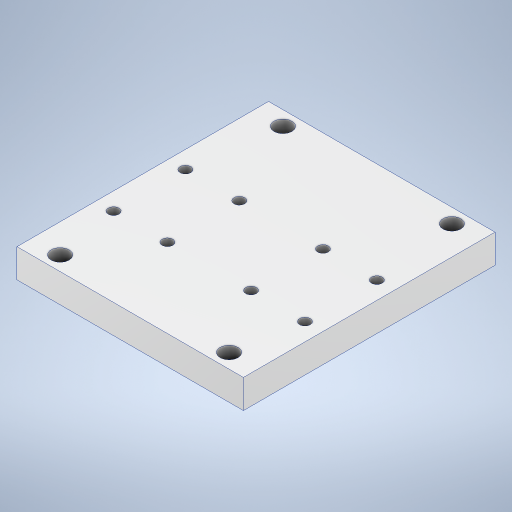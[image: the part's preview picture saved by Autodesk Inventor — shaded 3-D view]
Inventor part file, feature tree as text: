
AUTODESK INVENTOR PART (.ipt)
format: ipt  version: 2023 (Build 270158000, 158)  size: 260,096 bytes
history: native  units: mm
features: sketch x3, hole x2, extrude x1
ambient origin geometry x8: Origin, YZ Plane, XZ Plane, XY Plane, X Axis, Y Axis, Z Axis, Center Point
bodies: Solid1 (feature_tree)
feature tree (6):
  extrude  "Extrusion1"  Depth=63.0mm
  hole  "Hole1"  [1 undecoded]
  hole  "Hole2"  [1 undecoded]
  sketch  "Sketch1"  dims[d0=70.0mm d1=63.0mm]
  sketch  "Sketch2"  dims[d2=8.0mm d3=0.0mm d4=70.0mm]
  sketch  "Sketch3"  dims[d5=63.0mm d6=20.0mm d8=15.0mm d9=20.0mm d11=20.0mm d16=20.0mm d18=20.0mm d19=20.0mm d21=15.0mm d24=23.25mm d25=0.0mm d26=28.0mm d27=53.25mm d28=-4.875mm d29=3.0mm d30=6.0mm d31=4.0mm d32=2.0mm d33=90.0deg d34=0.5mm d35=20.594885mm d36=20.0mm d38=47.0mm d39=20.0mm d41=62.0mm d44=63.0mm d45=70.0mm d46=4.0mm d47=8.0mm d48=5.0mm d49=10.0mm d50=3.023mm d51=2.0mm d52=14.3117mm d53=0.5mm d54=20.594885mm]
note: 2 required parameter values undecoded (feature->parameter linkage not recoverable at this tier; creation-order binding heuristic only, values carry confidence <= 0.55)
